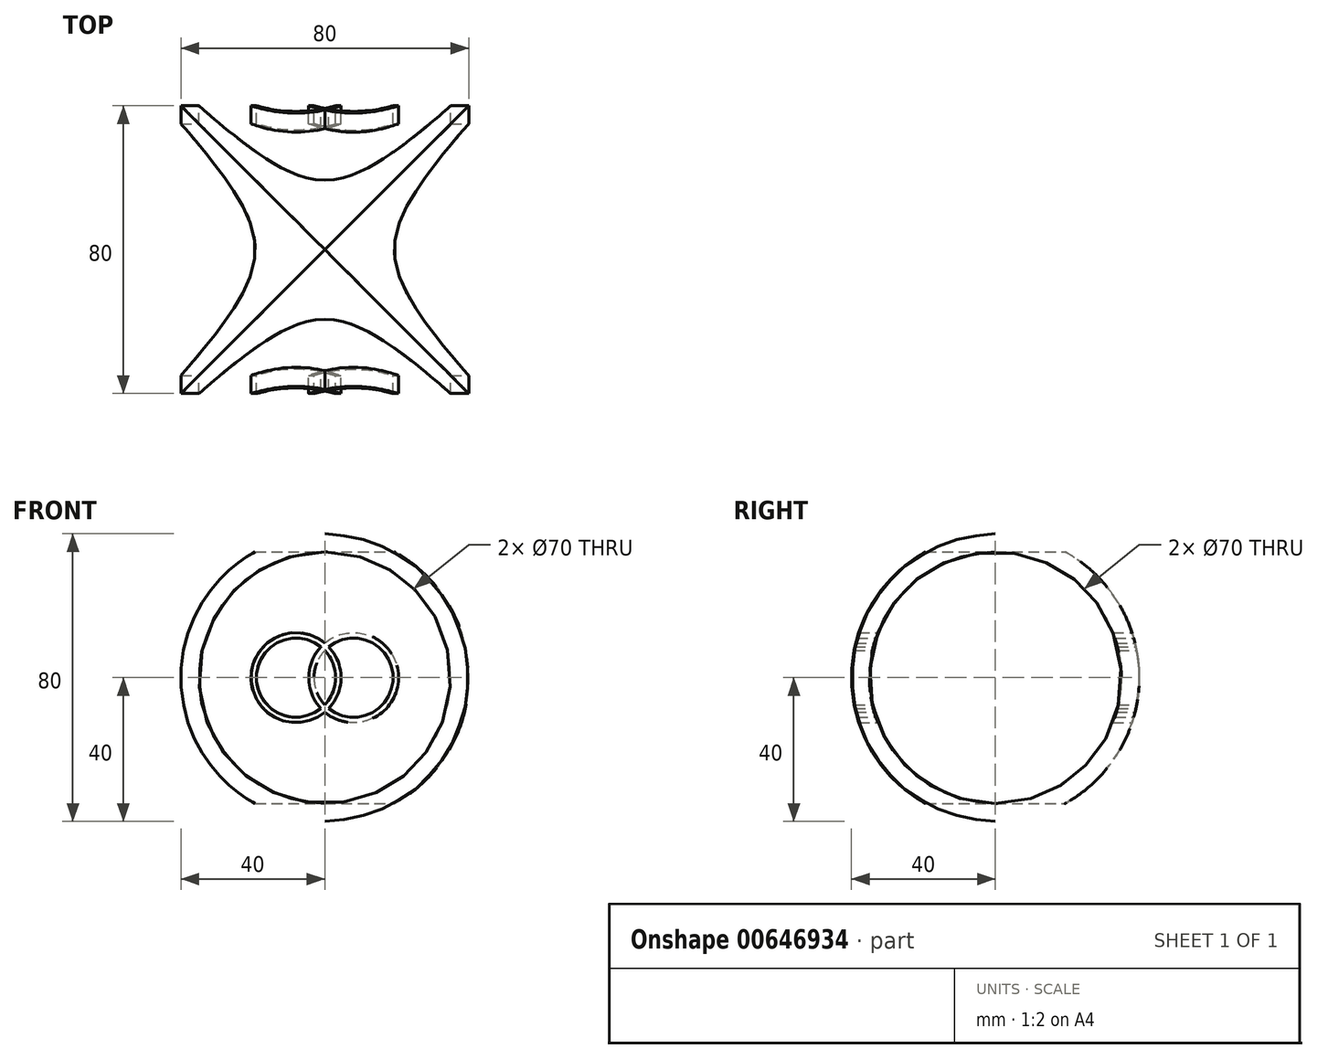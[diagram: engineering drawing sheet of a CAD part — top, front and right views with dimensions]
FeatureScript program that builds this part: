
annotation { "Feature Type Name" : "Feature", "Feature Type Description" : "" }
export const myFeature = defineFeature(function(context is Context, id is Id, definition is map)
    precondition{}
    {
        {
            var Q0;
            Q0=qCreatedBy(makeId("Top.planeOp"),FACE);
            var sketch = newSketch(context, id + "F0", { "sketchPlane" : qUnion([Q0])});
            skLineSegment(sketch, "E0.bottom", {"start": v(-40, -40) * mm, "end": v(40, -40) * mm});
            skLineSegment(sketch, "E0.top", {"start": v(-40, 40) * mm, "end": v(40, 40) * mm});
            skLineSegment(sketch, "E0.left", {"start": v(-40, -40) * mm, "end": v(-40, 40) * mm});
            skLineSegment(sketch, "E0.right", {"start": v(40, -40) * mm, "end": v(40, 40) * mm});
            skLineSegment(sketch, "E1", {"start": v(40, 0) * mm, "end": v(0, 0) * mm, "construction": true});
            skLineSegment(sketch, "E2", {"start": v(0, 0) * mm, "end": v(0, -40) * mm, "construction": true});
            skSolve(sketch);
        }
        {
            var Q0;
            Q0=makeQuery(id+"F0.imprint","IMPRINT",FACE,{"disambiguationData":[TD([[makeQuery(id+"F0.imprint","IMPRINT",EDGE,{"derivedFrom":sQuery(id+"F0.wireOp",EDGE,"E0.bottom")}),1.0]])]});
            extrude(context, id + "F1", {"entities" : qUnion([Q0]), "endBound" : BoundingType.SYMMETRIC, "depth" : 80 * mm, "offsetDistance" : 25 * mm});
        }
        {
            var Q0;
            Q0=makeQuery(id+"F1.opExtrude","SWEPT_FACE",FACE,{"disambiguationData":[OSD([sQuery(id+"F0.wireOp",EDGE,"E0.right")])]});
            var sketch = newSketch(context, id + "F2", { "sketchPlane" : qUnion([Q0])});
            skCircle(sketch, "E3", {"center": v(0, 0) * mm, "radius": 40 * mm});
            skSolve(sketch);
        }
        {
            var Q0;
            {var subQ0=sQuery(id+"F2.wireOp",EDGE,"E3");var subQ1=sQuery(id+"F0.wireOp",EDGE,"E0.right");var subQ2=makeQuery(id+"F1.opExtrude","CAP_EDGE",EDGE,{"disambiguationData":[OSD([subQ1])],"isStart":false});var subQ3=makeQuery(id+"F2.imprint","INTERSECT",VERTEX,{"derivedFrom":[subQ2,subQ0]});Q0=makeQuery(id+"F2.imprint","IMPRINT",FACE,{"disambiguationData":[TD([[makeQuery(id+"F2.imprint","IMPRINT",EDGE,{"disambiguationData":[TD([[subQ3,-1.0]])],"derivedFrom":subQ0}),-1.0]])]});}
            var Q1;
            {var subQ0=sQuery(id+"F2.wireOp",EDGE,"E3");var subQ1=sQuery(id+"F0.wireOp",EDGE,"E0.right");var subQ2=makeQuery(id+"F1.opExtrude","CAP_EDGE",EDGE,{"disambiguationData":[OSD([subQ1])],"isStart":false});var subQ3=makeQuery(id+"F2.imprint","INTERSECT",VERTEX,{"derivedFrom":[subQ2,subQ0]});Q1=makeQuery(id+"F2.imprint","IMPRINT",FACE,{"disambiguationData":[TD([[makeQuery(id+"F2.imprint","IMPRINT",EDGE,{"disambiguationData":[TD([[subQ3,1.0]])],"derivedFrom":subQ0}),-1.0]])]});}
            var Q2;
            {var subQ0=sQuery(id+"F2.wireOp",EDGE,"E3");var subQ1=sQuery(id+"F0.wireOp",EDGE,"E0.right");var subQ4=makeQuery(id+"F1.opExtrude","CAP_EDGE",EDGE,{"disambiguationData":[OSD([subQ1])],"isStart":true});var subQ5=makeQuery(id+"F2.imprint","INTERSECT",VERTEX,{"derivedFrom":[subQ4,subQ0]});Q2=makeQuery(id+"F2.imprint","IMPRINT",FACE,{"disambiguationData":[TD([[makeQuery(id+"F2.imprint","IMPRINT",EDGE,{"disambiguationData":[TD([[subQ5,-1.0]])],"derivedFrom":subQ0}),-1.0]])]});}
            var Q3;
            {var subQ0=sQuery(id+"F2.wireOp",EDGE,"E3");var subQ1=sQuery(id+"F0.wireOp",EDGE,"E0.right");var subQ4=makeQuery(id+"F1.opExtrude","CAP_EDGE",EDGE,{"disambiguationData":[OSD([subQ1])],"isStart":true});var subQ5=makeQuery(id+"F2.imprint","INTERSECT",VERTEX,{"derivedFrom":[subQ4,subQ0]});Q3=makeQuery(id+"F2.imprint","IMPRINT",FACE,{"disambiguationData":[TD([[makeQuery(id+"F2.imprint","IMPRINT",EDGE,{"disambiguationData":[TD([[subQ5,1.0]])],"derivedFrom":subQ0}),-1.0]])]});}
            var Q4;
            Q4=makeQuery(id+"F1.opExtrude","SWEPT_FACE",FACE,{"disambiguationData":[OSD([sQuery(id+"F0.wireOp",EDGE,"E0.left")])]});
            extrude(context, id + "F3", {"entities" : qUnion([Q0, Q1, Q2, Q3, Q4]), "operationType" : NewBodyOperationType.REMOVE, "oppositeDirection" : true, "depth" : 90 * mm, "offsetDistance" : 25 * mm});
        }
        {
            var Q0;
            Q0=qCreatedBy(makeId("Front.planeOp"),FACE);
            var sketch = newSketch(context, id + "F4", { "sketchPlane" : qUnion([Q0])});
            skCircle(sketch, "E4", {"center": v(0, 0) * mm, "radius": 40 * mm});
            skLineSegment(sketch, "E5.bottom", {"start": v(-53.81, 53.19) * mm, "end": v(60.08, 53.19) * mm});
            skLineSegment(sketch, "E5.top", {"start": v(-53.81, -52.65) * mm, "end": v(60.08, -52.65) * mm});
            skLineSegment(sketch, "E5.left", {"start": v(-53.81, 53.19) * mm, "end": v(-53.81, -52.65) * mm});
            skLineSegment(sketch, "E5.right", {"start": v(60.08, 53.19) * mm, "end": v(60.08, -52.65) * mm});
            skSolve(sketch);
        }
        {
            var Q0;
            Q0=makeQuery(id+"F4.imprint","IMPRINT",FACE,{"disambiguationData":[TD([[makeQuery(id+"F4.imprint","IMPRINT",EDGE,{"derivedFrom":sQuery(id+"F4.wireOp",EDGE,"E5.bottom")}),-1.0]])]});
            extrude(context, id + "F5", {"entities" : qUnion([Q0]), "operationType" : NewBodyOperationType.REMOVE, "endBound" : BoundingType.SYMMETRIC, "oppositeDirection" : true, "depth" : 100 * mm, "offsetDistance" : 25 * mm});
        }
        {
            var Q0;
            Q0=qCreatedBy(makeId("Front.planeOp"),FACE);
            var sketch = newSketch(context, id + "F6", { "sketchPlane" : qUnion([Q0])});
            skCircle(sketch, "E6", {"center": v(0, 0) * mm, "radius": 35 * mm});
            skCircle(sketch, "E7", {"center": v(-8, 0) * mm, "radius": 12.5 * mm});
            skCircle(sketch, "E8", {"center": v(8, 0) * mm, "radius": 12.5 * mm});
            skSolve(sketch);
        }
        {
            var Q0;
            Q0 = qSketchRegion(id + "F6", true);
            extrude(context, id + "F7", {"entities" : qUnion([Q0]), "operationType" : NewBodyOperationType.REMOVE, "endBound" : BoundingType.SYMMETRIC, "depth" : 150 * mm, "offsetDistance" : 25 * mm});
        }
        {
            var Q0;
            Q0=qCreatedBy(makeId("Right.planeOp"),FACE);
            var sketch = newSketch(context, id + "F8", { "sketchPlane" : qUnion([Q0])});
            skCircle(sketch, "E9", {"center": v(0, 0) * mm, "radius": 35 * mm});
            skSolve(sketch);
        }
        {
            var Q0;
            Q0 = qSketchRegion(id + "F8", true);
            extrude(context, id + "F9", {"entities" : qUnion([Q0]), "operationType" : NewBodyOperationType.REMOVE, "endBound" : BoundingType.SYMMETRIC, "oppositeDirection" : true, "depth" : 150 * mm, "offsetDistance" : 25 * mm});
        }
        {
            var Q0;
            Q0=qCreatedBy(makeId("Front.planeOp"),FACE);
            var sketch = newSketch(context, id + "F10", { "sketchPlane" : qUnion([Q0])});
            skArc(sketch, "E10", {"start": v(0, -7.55) * mm, "mid": v(3, 0) * mm, "end": v(0, 7.55) * mm});
            skArc(sketch, "E11", {"start": v(1.1, -8.57) * mm, "mid": v(19, 0) * mm, "end": v(1.1, 8.57) * mm});
            skArc(sketch, "E12", {"start": v(1.1, -8.57) * mm, "mid": v(4.5, 0) * mm, "end": v(1.1, 8.57) * mm});
            skArc(sketch, "E13.trimOffspring", {"start": v(0, 7.55) * mm, "mid": v(-3, 0) * mm, "end": v(0, -7.55) * mm});
            skArc(sketch, "E14.trimOffspring", {"start": v(-1.07, 8.54) * mm, "mid": v(-4.46, 0) * mm, "end": v(-1.07, -8.54) * mm});
            skArc(sketch, "E15.trimOffspring", {"start": v(-1.07, 8.54) * mm, "mid": v(-19, 0) * mm, "end": v(-1.07, -8.54) * mm});
            skSolve(sketch);
        }
        {
            var Q0;
            Q0 = qSketchRegion(id + "F10", true);
            extrude(context, id + "F11", {"entities" : qUnion([Q0]), "operationType" : NewBodyOperationType.REMOVE, "endBound" : BoundingType.SYMMETRIC, "depth" : 150 * mm, "offsetDistance" : 25 * mm});
        }
    });
